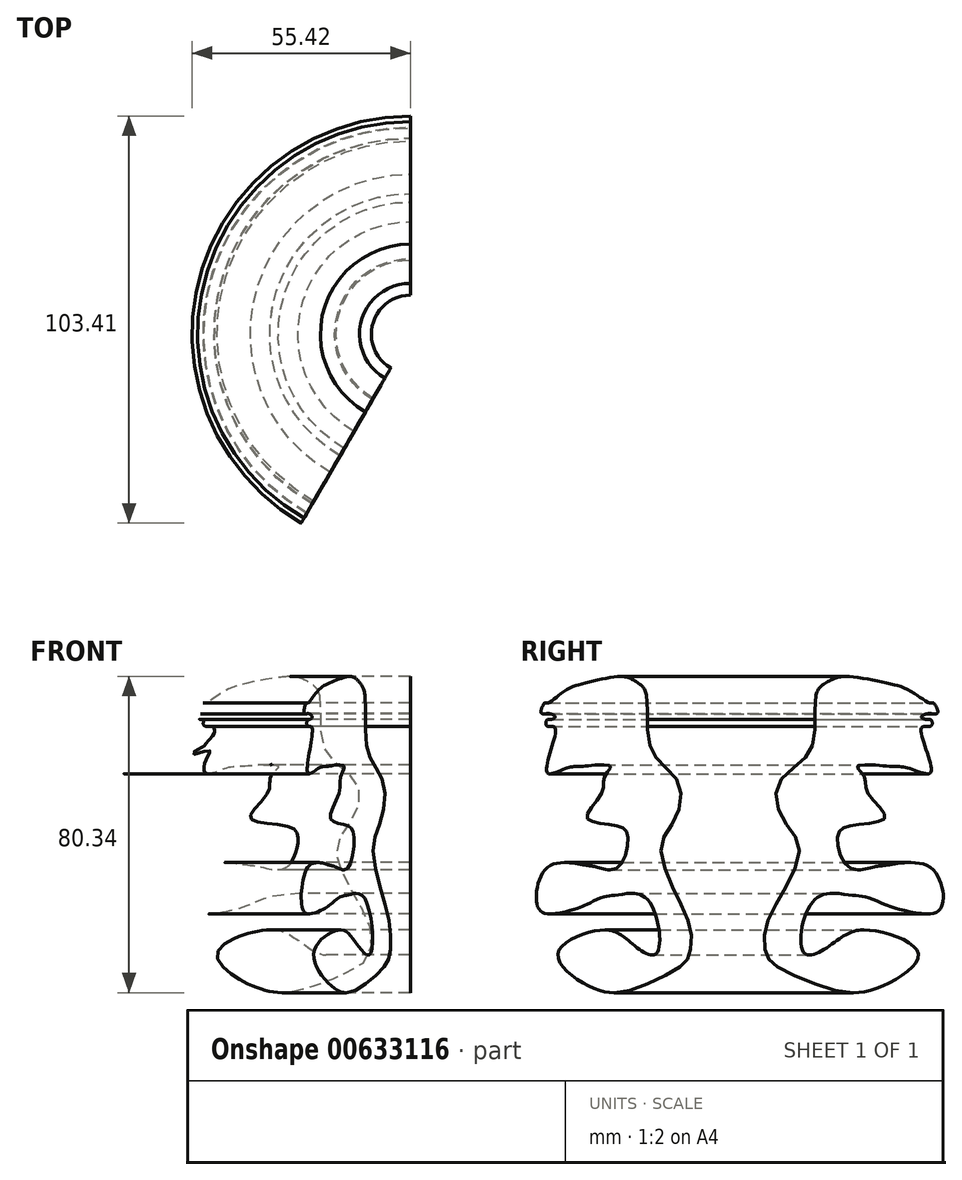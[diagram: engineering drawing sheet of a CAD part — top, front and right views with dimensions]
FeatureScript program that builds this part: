
annotation { "Feature Type Name" : "Feature", "Feature Type Description" : "" }
export const myFeature = defineFeature(function(context is Context, id is Id, definition is map)
    precondition{}
    {
        {
            var Q0;
            Q0=qCreatedBy(makeId("Top.planeOp"),FACE);
            var sketch = newSketch(context, id + "F0", { "sketchPlane" : qUnion([Q0])});
            skCircle(sketch, "E0", {"center": v(0, 0) * mm, "radius": 41.25 * mm});
            skSolve(sketch);
        }
        {
            var Q0;
            Q0=qCreatedBy(makeId("Right.planeOp"),FACE);
            var sketch = newSketch(context, id + "F1", { "sketchPlane" : qUnion([Q0])});
            skFitSpline(sketch, "E1", {"points": [v(23.1, 38.35) * mm, v(22.68, 28.06) * mm, v(19.6, 21.68) * mm, v(13.42, 15.5) * mm, v(14.65, 6.85) * mm, v(18.77, 0) * mm, v(14.86, -11.47) * mm, v(10.13, -21.35) * mm, v(10.54, -27.73) * mm, v(12.8, -30.4) * mm, v(26.18, -36.17) * mm, v(38.53, -36.17) * mm, v(49.03, -27.32) * mm, v(36.06, -21.35) * mm, v(28.45, -24.03) * mm, v(20.21, -27.32) * mm, v(22.68, -13.73) * mm, v(31.74, -12.5) * mm, v(35.45, -12.9) * mm, v(40.8, -14.97) * mm, v(43.89, -16) * mm, v(53.15, -17.03) * mm, v(55.42, -13.11) * mm, v(51.5, -5.09) * mm, v(41, -4.88) * mm, v(37.92, -5.3) * mm, v(31.54, -5.5) * mm, v(28.65, 2.74) * mm, v(32.15, 5.2) * mm, v(40.6, 7.27) * mm, v(36.06, 13.65) * mm, v(35.45, 17.56) * mm, v(33.6, 20.24) * mm, v(42.03, 20.24) * mm, v(47.18, 19.62) * mm, v(52.33, 18.8) * mm, v(49.86, 29.91) * mm, v(52.33, 30.53) * mm, v(52.33, 31.97) * mm, v(50.89, 32.18) * mm, v(49.86, 32.8) * mm, v(51.7, 33.62) * mm, v(53.97, 33.82) * mm, v(52.95, 36.3) * mm, v(52.12, 36.3) * mm, v(50.47, 37.12) * mm, v(48.42, 38.56) * mm, v(45.33, 40.2) * mm, v(42.65, 41.03) * mm, v(38.12, 42.06) * mm, v(32.77, 42.88) * mm, v(28.86, 42.88) * mm, v(24.95, 41.03) * mm, v(23.1, 38.35) * mm]});
            skSolve(sketch);
        }
        {
            var Q0;
            Q0=makeQuery(id+"F1.imprint","IMPRINT",FACE,{"disambiguationData":[TD([[makeQuery(id+"F1.imprint","IMPRINT",EDGE,{"derivedFrom":sQuery(id+"F1.wireOp",EDGE,"E1")}),1.0]])]});
            var Q1;
            Q1=sQuery(id+"F0.wireOp",EDGE,"E0");
            revolve(context, id + "F2", {"entities" : qUnion([Q0]), "axis" : qUnion([Q1]), "revolveType" : RevolveType.ONE_DIRECTION, "angle" : 150 * degree});
        }
    });
